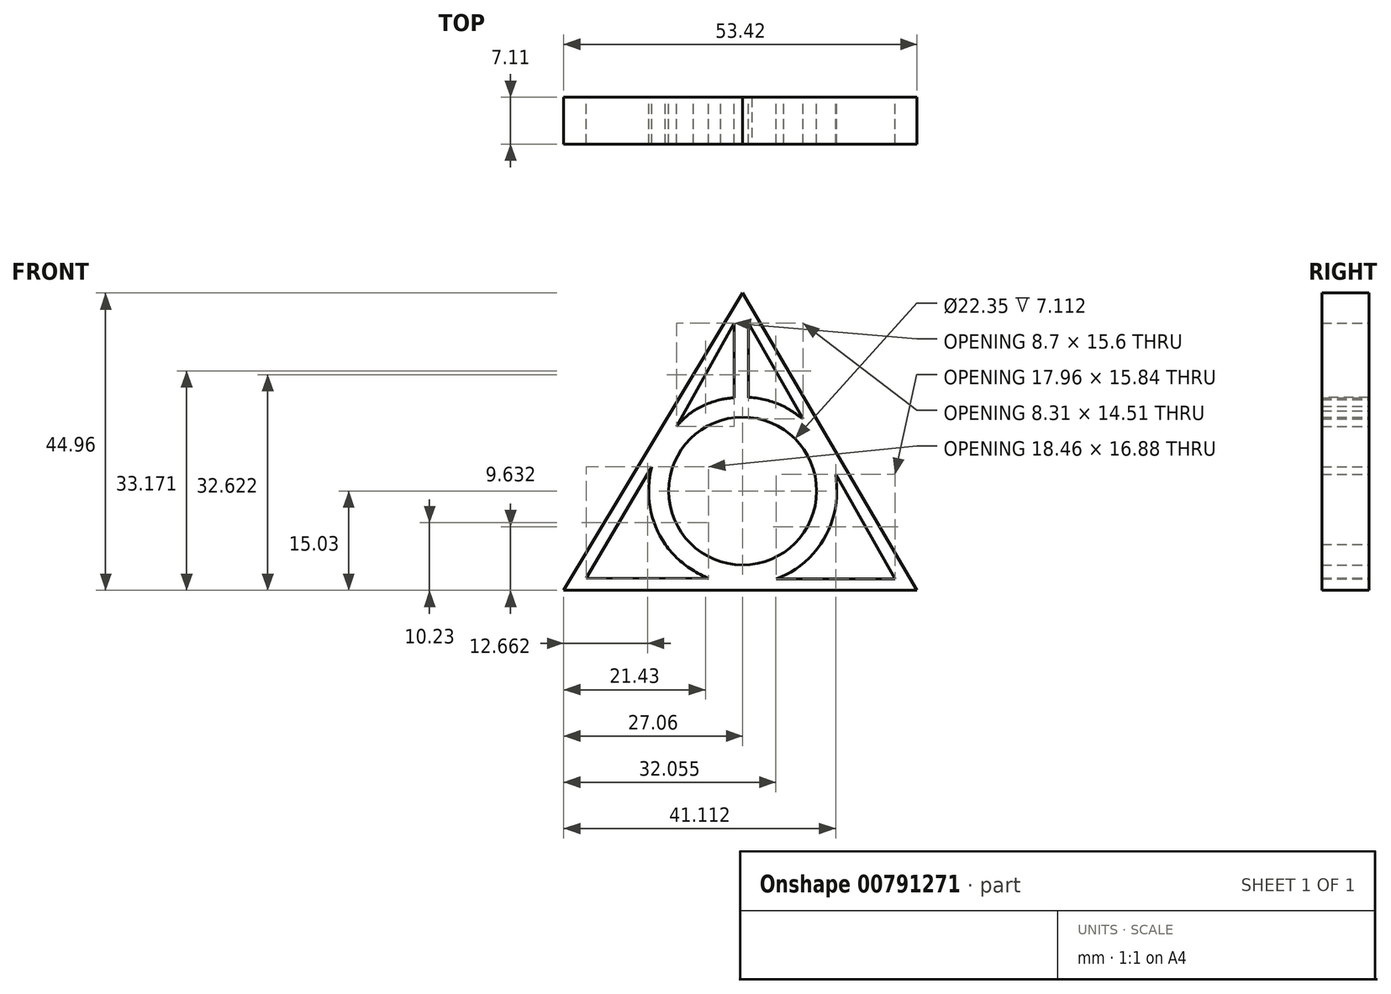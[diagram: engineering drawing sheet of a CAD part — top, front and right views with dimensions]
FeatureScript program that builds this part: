
annotation { "Feature Type Name" : "Feature", "Feature Type Description" : "" }
export const myFeature = defineFeature(function(context is Context, id is Id, definition is map)
    precondition{}
    {
        {
            var Q0;
            Q0=qCreatedBy(makeId("Front.planeOp"),FACE);
            var sketch = newSketch(context, id + "F0", { "sketchPlane" : qUnion([Q0])});
            skLineSegment(sketch, "E0", {"start": v(0, 29.93) * mm, "end": v(-27.06, -15.03) * mm});
            skLineSegment(sketch, "E1", {"start": v(0, 29.93) * mm, "end": v(26.36, -15.03) * mm});
            skFitSpline(sketch, "E2", {"points": [v(-23.63, -13.17) * mm, v(-5.17, -13.24) * mm], "startDerivative": vector(18.46, -0.07) * mm, "endDerivative": vector(18.46, -0.07) * mm});
            skFitSpline(sketch, "E3", {"points": [v(-23.63, -13.17) * mm, v(-13.74, 3.64) * mm], "startDerivative": vector(9.9, 16.81) * mm, "endDerivative": vector(9.9, 16.81) * mm});
            skFitSpline(sketch, "E4", {"points": [v(-13.74, 3.64) * mm, v(-14.4, 0) * mm, v(-13.15, -5.46) * mm, v(-10.9, -9.09) * mm, v(-8.13, -11.6) * mm, v(-5.17, -13.24) * mm], "startDerivative": vector(-5.29, -17.83) * mm, "endDerivative": vector(16.6, -8.2) * mm});
            skLineSegment(sketch, "E5", {"start": v(23.03, -13.32) * mm, "end": v(14.1, 2.52) * mm});
            skLineSegment(sketch, "E6", {"start": v(23.03, -13.32) * mm, "end": v(5.07, -13.32) * mm});
            skFitSpline(sketch, "E7", {"points": [v(5.07, -13.32) * mm, v(8.29, -11.6) * mm, v(11.43, -8.53) * mm, v(13.23, -5.24) * mm, v(14.17, -1.4) * mm, v(14.1, 2.52) * mm], "startDerivative": vector(16.81, 7.66) * mm, "endDerivative": vector(-1.52, 19.6) * mm});
            skLineSegment(sketch, "E8", {"start": v(-1.28, 25.4) * mm, "end": v(-9.98, 9.79) * mm});
            skLineSegment(sketch, "E9", {"start": v(-1.28, 25.4) * mm, "end": v(-1.28, 14.1) * mm});
            skLineSegment(sketch, "E10", {"start": v(0.84, 25.4) * mm, "end": v(0.84, 14.1) * mm});
            skLineSegment(sketch, "E11", {"start": v(0.84, 25.4) * mm, "end": v(9.15, 10.89) * mm});
            skFitSpline(sketch, "E12", {"points": [v(-9.98, 9.79) * mm, v(-7.4, 12.14) * mm, v(-3.79, 13.71) * mm, v(-1.28, 14.1) * mm], "startDerivative": vector(6.82, 7.3) * mm, "endDerivative": vector(8.11, 0.79) * mm});
            skFitSpline(sketch, "E13", {"points": [v(9.15, 10.89) * mm, v(5.78, 13) * mm, v(2.49, 14.1) * mm, v(0.84, 14.1) * mm], "startDerivative": vector(-8.37, 5.88) * mm, "endDerivative": vector(-6.03, -0.54) * mm});
            skArc(sketch, "E14", {"start": v(-0.36, 29.98) * mm, "mid": v(-0.18, 29.96) * mm, "end": v(0, 29.93) * mm});
            skPoint(sketch, "E14.second.point", {"position": v(0, 60.54) * mm});
            skPoint(sketch, "E14.third.point", {"position": v(-0.36, 29.98) * mm});
            skArc(sketch, "E15", {"start": v(-13.74, 3.64) * mm, "mid": v(-12.67, -6.44) * mm, "end": v(-5.17, -13.24) * mm});
            skArc(sketch, "E16.trimOffspring", {"start": v(9.05, 10.96) * mm, "mid": v(-0.36, 14.2) * mm, "end": v(-9.6, 10.49) * mm});
            skLineSegment(sketch, "E17", {"start": v(-27.06, -15.03) * mm, "end": v(26.36, -15.03) * mm});
            skCircle(sketch, "E18", {"center": v(0, 0) * mm, "radius": 11.18 * mm});
            skSolve(sketch);
        }
        {
            var Q0;
            Q0 = qSketchRegion(id + "F0", true);
            extrude(context, id + "F1", {"entities" : qUnion([Q0]), "depth" : 7.11 * mm, "offsetDistance" : 25.4 * mm});
        }
    });
